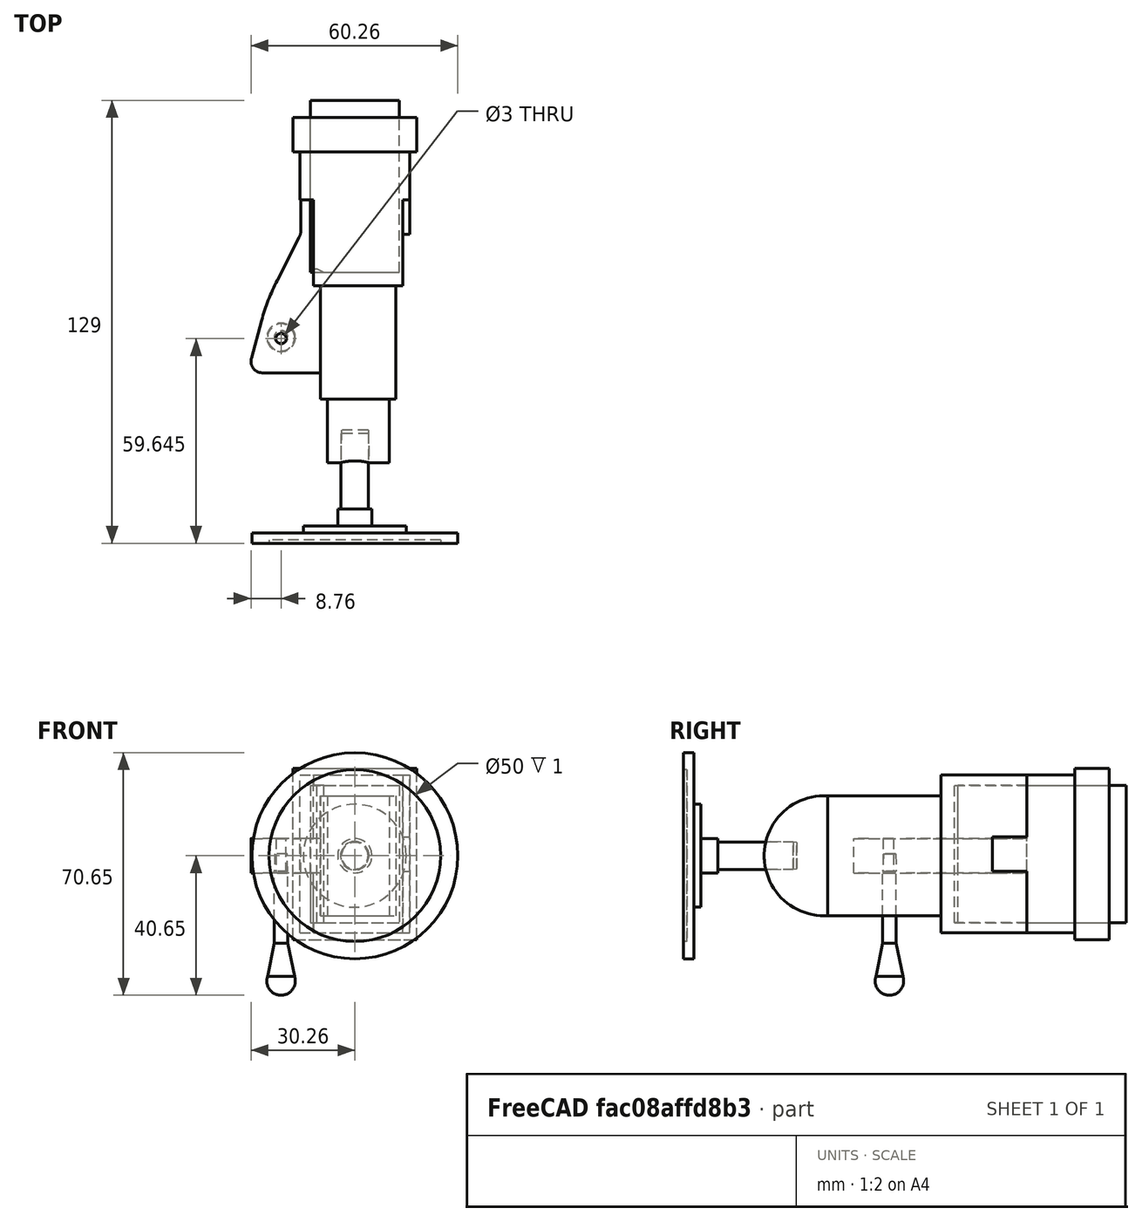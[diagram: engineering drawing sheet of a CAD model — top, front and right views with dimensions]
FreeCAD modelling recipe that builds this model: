
FCSTD DOCUMENT  (FreeCAD 0.16R6662 (Git))
Label: qtippholder-jw-csg-pocket
License: All rights reserved
LicenseURL: http://en.wikipedia.org/wiki/All_rights_reserved
objects: Part::Cylinder×7, Part::Box×6, Part::Cone×3, Part::MultiFuse×3, Part::Cut×3, Sketcher::SketchObject×2, App::DocumentObjectGroup×2, Mesh::Feature×1, PartDesign::Pad×1, Part::Sphere×1, PartDesign::Pocket×1
note: 29 computed .brp shape members not serialized (recipe doc carries the construction recipe); baked Part::Feature solids carry a one-line shape summary decoded from their .brp

FEATURE [Mesh::Feature] EarClnrHldr
  Placement = pos=(1.7939,1.69608,-3.31283) rot=(0,0,1;0rad)
FEATURE [Part::Box] Box  label="hut"
  Height = 50
  Length = 36
  Placement = pos=(14,116,11) rot=(0,0,1;0rad)
  Width = 10
FEATURE [Part::Box] Box001  label="stirn"
  Height = 46
  Length = 32
  Placement = pos=(16,102,13) rot=(0,0,1;0rad)
  Width = 17
FEATURE [Part::Box] Box002  label="gnack"
  Height = 10
  Length = 26
  Placement = pos=(22,92,31) rot=(0,0,1;0rad)
  Width = 12
FEATURE [Part::Box] Box003  label="augen"
  Height = 46
  Length = 26
  Placement = pos=(20,77,13) rot=(0,0,1;0rad)
  Width = 26
FEATURE [Part::Box] Box004  label="wangen"
  Height = 35
  Length = 22
  Placement = pos=(22,44,18) rot=(0,0,1;0rad)
  Width = 36
FEATURE [Part::Cylinder] Cylinder  label="kinn"
  Angle = 360
  Height = 18
  Placement = pos=(24,43,35.5) rot=(0,1,0;1.5708rad)
  Radius = 17.5
FEATURE [Sketcher::SketchObject] Sketch001
  Placement = pos=(22,44,36) rot=(0,0,1;0rad)
  sketch-geometry (10):
    g0: LineSegment StartX=1.5 StartY=7.67084 StartZ=0 EndX=-16.9205 EndY=7.67084 EndZ=0
    g1: LineSegment StartX=-20.1462 StartY=11.8885 StartZ=0 EndX=-17.1712 EndY=22.8519 EndZ=0
    g2: LineSegment StartX=-12.6256 StartY=34.6 StartZ=0 EndX=-6.24014 EndY=47.0658 EndZ=0
    g3: LineSegment StartX=-5.70418 StartY=49.2877 StartZ=0 EndX=-5.70418 EndY=58.874 EndZ=0
    g4: LineSegment StartX=-5.70418 StartY=58.874 StartZ=0 EndX=1.5 EndY=58.874 EndZ=0
    g5: LineSegment StartX=1.5 StartY=58.874 StartZ=0 EndX=1.5 EndY=7.67084 EndZ=0
    g6: ArcOfCircle CenterX=-16.9205 CenterY=11.0132 CenterZ=0 NormalX=0 NormalY=0 NormalZ=1 Radius=3.34236 StartAngle=2.87662 EndAngle=4.71239
    g7: ArcOfCircle CenterX=41.2664 CenterY=6.99453 CenterZ=0 NormalX=0 NormalY=0 NormalZ=1 Radius=60.5508 StartAngle=2.6682 EndAngle=2.87662
    g8: ArcOfCircle CenterX=-10.5778 CenterY=49.2877 CenterZ=0 NormalX=0 NormalY=0 NormalZ=1 Radius=4.87365 StartAngle=5.8098 EndAngle=6.28319
    g9: Circle CenterX=-11.5 CenterY=17.6445 CenterZ=0 NormalX=0 NormalY=0 NormalZ=1 Radius=1.5
  constraints (14):
    c: Horizontal(g0)
    c: Vertical(g3)
    c: Coincident(g3,g4)
    c: Horizontal(g4)
    c: Coincident(g4,g5)
    c: Coincident(g5,g0)
    c: Vertical(g5)
    c: Tangent(g0,g6) = 1.5708
    c: Tangent(g1,g6) = 1.5708
    c: Tangent(g1,g7) = 1.5708
    c: Tangent(g2,g7) = 1.5708
    c: Tangent(g2,g8) = -1.5708
    c: Tangent(g3,g8) = -1.5708
    c: Radius(g9) = 1.5
FEATURE [PartDesign::Pad] Pad  label="nase"
  Length = 4.5
  Length2 = 5.5
  Placement = pos=(22,44,36) rot=(0,0,1;0rad)
  Sketch = -> Sketch001
  Type = 4
FEATURE [Part::Cylinder] Cylinder002  label="bein006"
  Angle = 360
  Height = 32
  Placement = pos=(32,34,35.5) rot=(1,0,0;1.5708rad)
  Radius = 4
FEATURE [Part::Cylinder] Cylinder003  label="bein001"
  Angle = 360
  Height = 11
  Placement = pos=(32,12,35.5) rot=(1,0,0;1.5708rad)
  Radius = 5
FEATURE [Part::Cylinder] Cylinder004  label="bein002"
  Angle = 360
  Height = 4
  Placement = pos=(32,7,35.5) rot=(1,0,0;1.5708rad)
  Radius = 15
FEATURE [Part::Cylinder] Cylinder005  label="bein003"
  Angle = 360
  Height = 3
  Placement = pos=(32,5,35.5) rot=(1,0,0;1.5708rad)
  Radius = 30
FEATURE [Part::Cylinder] Cylinder006  label="bein004"
  Angle = 360
  Height = 3
  Placement = pos=(32,3,35.5) rot=(1,0,0;1.5708rad)
  Radius = 25
FEATURE [Part::Box] Box005  label="kopfloch"
  Height = 40
  Length = 26
  Placement = pos=(19,81,16) rot=(0,0,1;0rad)
  Width = 50
FEATURE [Part::Cylinder] Cylinder007  label="staebchen"
  Angle = 360
  Height = 27
  Placement = pos=(10.5,62,4) rot=(0,0,1;0rad)
  Radius = 2
FEATURE [Part::Sphere] Sphere  label="Kugel"
  Angle1 = -90
  Angle2 = 90
  Angle3 = 360
  Placement = pos=(10.5,62,-1) rot=(0,0,1;0rad)
  Radius = 4.15
FEATURE [Part::Cone] Cone  label="Kegel"
  Angle = 360
  Height = 10
  Placement = pos=(10.5,62,0) rot=(0,0,1;0rad)
  Radius1 = 4
  Radius2 = 2
FEATURE [Part::Cone] Cone001  label="Kegel001"
  Angle = 360
  Height = 5
  Placement = pos=(10.5,62,31) rot=(0,0,1;0rad)
  Radius1 = 2
  Radius2 = 1.8
FEATURE [Part::Cone] Cone002  label="beinloch001"
  Angle = 360
  Height = 11
  Placement = pos=(32,35,35.5) rot=(1,0,0;1.5708rad)
  Radius1 = 3.9
  Radius2 = 4.2
FEATURE [Part::MultiFuse] Fusion
  Shapes = -> [Box,Box001,Box002,Box003,Box004,Cylinder,Pad]
FEATURE [Part::MultiFuse] Fusion001
  Shapes = -> [Cone001,Cylinder007,Sphere,Cone]
FEATURE [App::DocumentObjectGroup] Gruppe001  label="halb-qtipp"
  Group = -> [Fusion001]
FEATURE [Part::MultiFuse] Fusion002
  Shapes = -> [Cylinder002,Cylinder003,Cylinder005,Cylinder004]
FEATURE [Part::Cut] Cut002
  Base = -> Fusion002
  Tool = -> Cylinder006
FEATURE [App::DocumentObjectGroup] Gruppe  label="bein"
  Group = -> [Cut002]
FEATURE [Sketcher::SketchObject] Sketch
  Placement = pos=(19,81,16) rot=(1,0,0;3.14159rad)
  Support = -> Box005 [Face5]
  sketch-geometry (4):
    g0: LineSegment StartX=0 StartY=0 StartZ=0 EndX=0 EndY=-1 EndZ=0
    g1: LineSegment StartX=0 StartY=-1 StartZ=0 EndX=2 EndY=-1 EndZ=0
    g2: LineSegment StartX=2 StartY=-1 StartZ=0 EndX=4 EndY=0 EndZ=0
    g3: LineSegment StartX=4 StartY=0 StartZ=0 EndX=0 EndY=0 EndZ=0
  constraints (11):
    c: Coincident(g-1,g0)
    c: PointOnObject(g0,g-2)
    c: Coincident(g0,g1)
    c: Horizontal(g1)
    c: Coincident(g1,g2)
    c: Coincident(g2,g3)
    c: Coincident(g3,g0)
    c: Horizontal(g3)
    c: DistanceY(g0,g0) = 1
    c: DistanceX(g1,g1) = 2
    c: DistanceX(g3,g3) = 4
FEATURE [PartDesign::Pocket] Pocket
  Length = 5
  Placement = pos=(19,81,16) rot=(0,0,1;0rad)
  Sketch = -> Sketch
  Type = 1
FEATURE [Part::Cut] Cut
  Base = -> Fusion
  Tool = -> Pocket
FEATURE [Part::Cut] Cut003  label="kopf"
  Base = -> Cut
  Tool = -> Cone002
